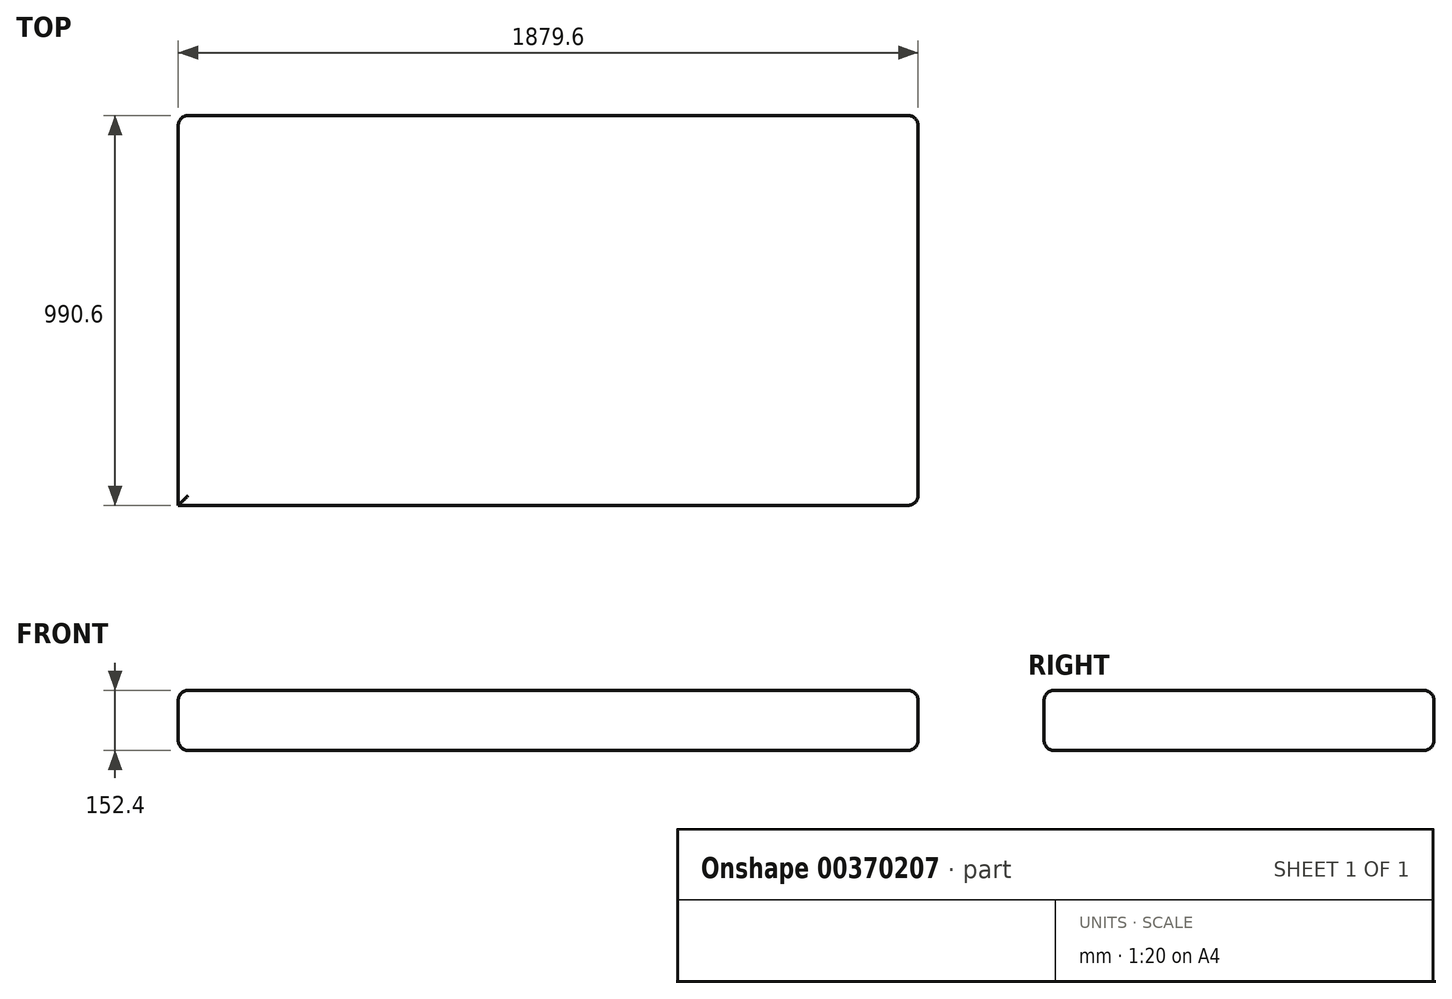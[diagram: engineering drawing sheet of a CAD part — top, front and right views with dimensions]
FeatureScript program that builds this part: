
annotation { "Feature Type Name" : "Feature", "Feature Type Description" : "" }
export const myFeature = defineFeature(function(context is Context, id is Id, definition is map)
    precondition{}
    {
        {
            var Q0;
            Q0=qCreatedBy(makeId("Top.planeOp"),FACE);
            var sketch = newSketch(context, id + "F0", { "sketchPlane" : qUnion([Q0])});
            skLineSegment(sketch, "E0.bottom", {"start": v(-937.91, 515.56) * mm, "end": v(941.69, 515.56) * mm});
            skLineSegment(sketch, "E0.top", {"start": v(-937.91, -475.04) * mm, "end": v(941.69, -475.04) * mm});
            skLineSegment(sketch, "E0.left", {"start": v(-937.91, 515.56) * mm, "end": v(-937.91, -475.04) * mm});
            skLineSegment(sketch, "E0.right", {"start": v(941.69, 515.56) * mm, "end": v(941.69, -475.04) * mm});
            skSolve(sketch);
        }
        {
            var Q0;
            Q0=makeQuery(id+"F0.imprint","IMPRINT",FACE,{"disambiguationData":[TD([[makeQuery(id+"F0.imprint","IMPRINT",EDGE,{"derivedFrom":sQuery(id+"F0.wireOp",EDGE,"E0.bottom")}),-1.0]])]});
            extrude(context, id + "F1", {"entities" : qUnion([Q0]), "depth" : 152.4 * mm});
        }
        {
            var Q0;
            Q0=makeQuery(id+"F1.opExtrude","CAP_EDGE",EDGE,{"disambiguationData":[OSD([sQuery(id+"F0.wireOp",EDGE,"E0.left")])],"isStart":false});
            var Q1;
            Q1=makeQuery(id+"F1.opExtrude","CAP_EDGE",EDGE,{"disambiguationData":[OSD([sQuery(id+"F0.wireOp",EDGE,"E0.top")])],"isStart":false});
            var Q2;
            Q2=makeQuery(id+"F1.opExtrude","CAP_EDGE",EDGE,{"disambiguationData":[OSD([sQuery(id+"F0.wireOp",EDGE,"E0.bottom")])],"isStart":false});
            var Q3;
            Q3=makeQuery(id+"F1.opExtrude","CAP_EDGE",EDGE,{"disambiguationData":[OSD([sQuery(id+"F0.wireOp",EDGE,"E0.right")])],"isStart":false});
            var Q4;
            Q4=makeQuery(id+"F1.opExtrude","CAP_EDGE",EDGE,{"disambiguationData":[OSD([sQuery(id+"F0.wireOp",EDGE,"E0.top")])],"isStart":true});
            var Q5;
            Q5=makeQuery(id+"F1.opExtrude","CAP_EDGE",EDGE,{"disambiguationData":[OSD([sQuery(id+"F0.wireOp",EDGE,"E0.left")])],"isStart":true});
            var Q6;
            Q6=makeQuery(id+"F1.opExtrude","CAP_EDGE",EDGE,{"disambiguationData":[OSD([sQuery(id+"F0.wireOp",EDGE,"E0.bottom")])],"isStart":true});
            var Q7;
            Q7=makeQuery(id+"F1.opExtrude","CAP_EDGE",EDGE,{"disambiguationData":[OSD([sQuery(id+"F0.wireOp",EDGE,"E0.right")])],"isStart":true});
            var Q8;
            Q8=makeQuery(id+"F1.opExtrude","SWEPT_EDGE",EDGE,{"disambiguationData":[OSD([sQuery(id+"F0.wireOp",EDGE,"E0.top"),sQuery(id+"F0.wireOp",EDGE,"E0.right")])]});
            var Q9;
            Q9=makeQuery(id+"F1.opExtrude","SWEPT_EDGE",EDGE,{"disambiguationData":[OSD([sQuery(id+"F0.wireOp",EDGE,"E0.bottom"),sQuery(id+"F0.wireOp",EDGE,"E0.right")])]});
            var Q10;
            Q10=makeQuery(id+"F1.opExtrude","SWEPT_EDGE",EDGE,{"disambiguationData":[OSD([sQuery(id+"F0.wireOp",EDGE,"E0.bottom"),sQuery(id+"F0.wireOp",EDGE,"E0.left")])]});
            fillet(context, id + "F2", {"entities" : qUnion([Q0, Q1, Q2, Q3, Q4, Q5, Q6, Q7, Q8, Q9, Q10]), "radius" : 25.4 * mm, "tangentPropagation" : true, "allowEdgeOverflow" : false});
        }
    });
